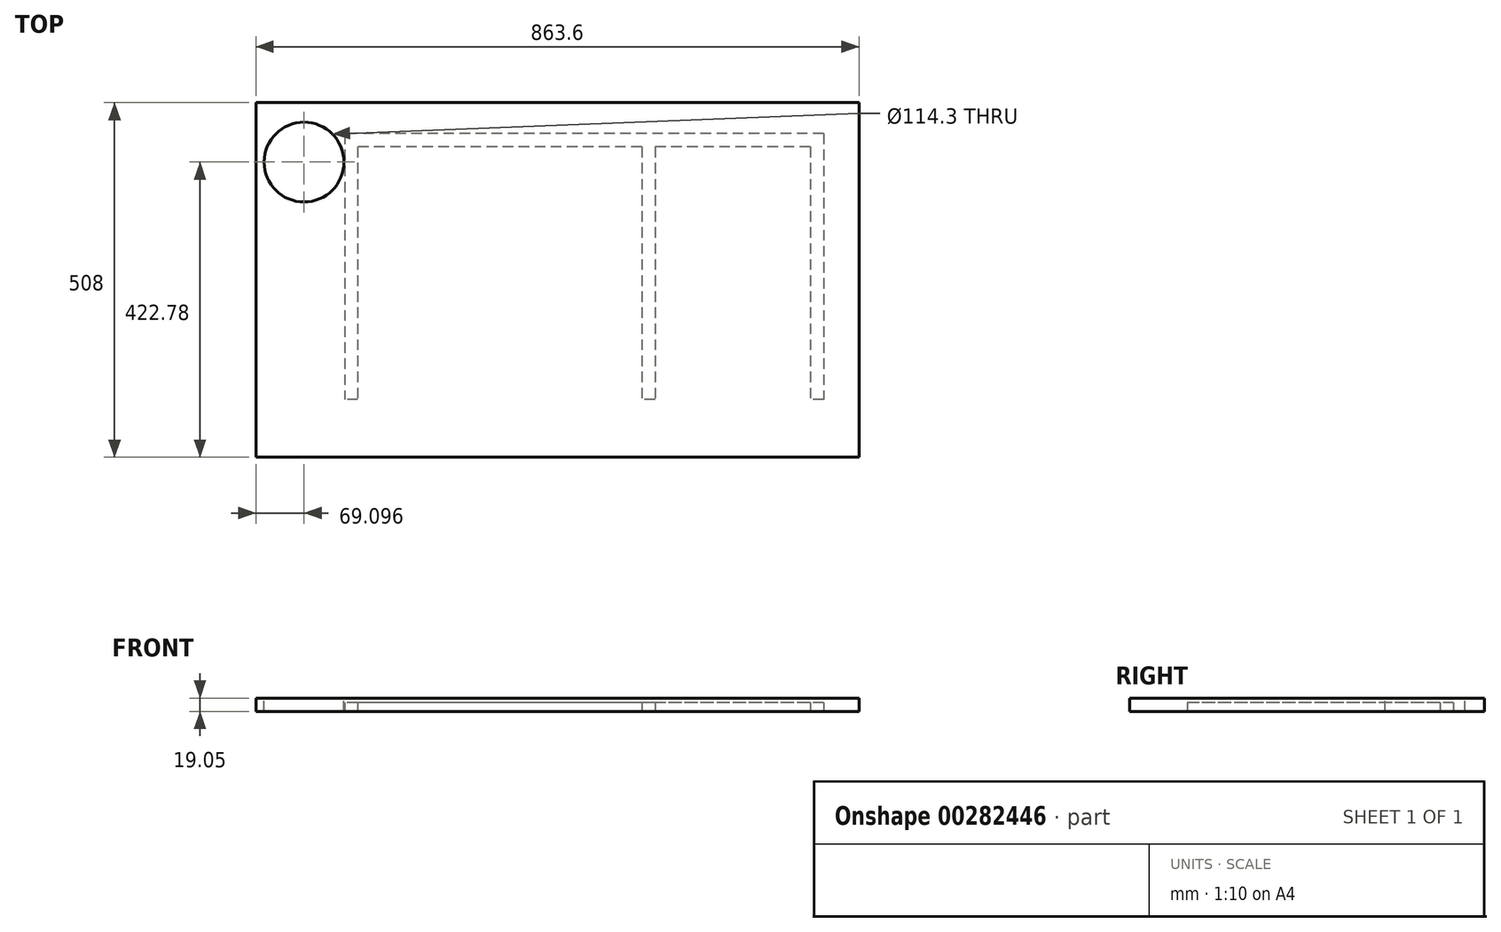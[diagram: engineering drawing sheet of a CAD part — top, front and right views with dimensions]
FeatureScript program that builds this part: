
annotation { "Feature Type Name" : "Feature", "Feature Type Description" : "" }
export const myFeature = defineFeature(function(context is Context, id is Id, definition is map)
    precondition{}
    {
        {
            var Q0;
            Q0=qCreatedBy(makeId("Top.planeOp"),FACE);
            var sketch = newSketch(context, id + "F0", { "sketchPlane" : qUnion([Q0])});
            skPoint(sketch, "E0.middle", {"position": v(0, 0) * mm});
            skLineSegment(sketch, "E1.bottom", {"start": v(-431.8, -254) * mm, "end": v(431.8, -254) * mm});
            skLineSegment(sketch, "E1.top", {"start": v(-431.8, 254) * mm, "end": v(431.8, 254) * mm});
            skLineSegment(sketch, "E1.left", {"start": v(-431.8, -254) * mm, "end": v(-431.8, 254) * mm});
            skLineSegment(sketch, "E1.right", {"start": v(431.8, -254) * mm, "end": v(431.8, 254) * mm});
            skSolve(sketch);
        }
        {
            var Q0;
            Q0 = qSketchRegion(id + "F0", true);
            extrude(context, id + "F1", {"entities" : qUnion([Q0]), "depth" : 19.05 * mm});
        }
        {
            var Q0;
            Q0=makeQuery(id+"F1.opExtrude","CAP_FACE",FACE,{"disambiguationData":[OSD([sQuery(id+"F0.wireOp",EDGE,"E1.bottom"),sQuery(id+"F0.wireOp",EDGE,"E1.top"),sQuery(id+"F0.wireOp",EDGE,"E1.left"),sQuery(id+"F0.wireOp",EDGE,"E1.right")])],"isStart":true});
            var sketch = newSketch(context, id + "F2", { "sketchPlane" : qUnion([Q0])});
            skLineSegment(sketch, "E2", {"start": v(0, -254) * mm, "end": v(0, 254) * mm, "construction": true});
            skLineSegment(sketch, "E3", {"start": v(431.8, 0) * mm, "end": v(-431.8, 0) * mm, "construction": true});
            skLineSegment(sketch, "E4", {"start": v(431.8, -254) * mm, "end": v(431.8, -209.55) * mm, "construction": true});
            skLineSegment(sketch, "E5", {"start": v(431.8, -209.55) * mm, "end": v(-431.8, -209.55) * mm, "construction": true});
            skLineSegment(sketch, "E6", {"start": v(431.8, -171.75) * mm, "end": v(381, -171.75) * mm, "construction": true});
            skLineSegment(sketch, "E7", {"start": v(381, -254) * mm, "end": v(381, 254) * mm, "construction": true});
            skLineSegment(sketch, "E8", {"start": v(-431.8, -119.08) * mm, "end": v(-304.8, -119.08) * mm, "construction": true});
            skLineSegment(sketch, "E9", {"start": v(-304.8, -254) * mm, "end": v(-304.8, 254) * mm, "construction": true});
            skLineSegment(sketch, "E10.bottom", {"start": v(381, -209.55) * mm, "end": v(-304.8, -209.55) * mm});
            skLineSegment(sketch, "E10.top", {"start": v(381, -190.5) * mm, "end": v(-304.8, -190.5) * mm});
            skLineSegment(sketch, "E10.left", {"start": v(381, -209.55) * mm, "end": v(381, -190.5) * mm});
            skLineSegment(sketch, "E10.right", {"start": v(-304.8, -209.55) * mm, "end": v(-304.8, -190.5) * mm});
            skLineSegment(sketch, "E11", {"start": v(38.1, -209.55) * mm, "end": v(38.1, -190.5) * mm, "construction": true});
            skLineSegment(sketch, "E12.bottom", {"start": v(-285.75, -190.5) * mm, "end": v(-304.8, -190.5) * mm});
            skLineSegment(sketch, "E12.top", {"start": v(-285.75, 171.45) * mm, "end": v(-304.8, 171.45) * mm});
            skLineSegment(sketch, "E12.left", {"start": v(-285.75, -190.5) * mm, "end": v(-285.75, 171.45) * mm});
            skLineSegment(sketch, "E12.right", {"start": v(-304.8, -190.5) * mm, "end": v(-304.8, 171.45) * mm});
            skLineSegment(sketch, "E13", {"start": v(-285.75, -74.88) * mm, "end": v(120.65, -74.88) * mm, "construction": true});
            skLineSegment(sketch, "E14", {"start": v(120.65, -190.5) * mm, "end": v(120.65, 254) * mm, "construction": true});
            skLineSegment(sketch, "E15.bottom", {"start": v(139.7, -190.5) * mm, "end": v(120.65, -190.5) * mm});
            skLineSegment(sketch, "E15.top", {"start": v(139.7, 171.45) * mm, "end": v(120.65, 171.45) * mm});
            skLineSegment(sketch, "E15.left", {"start": v(139.7, -190.5) * mm, "end": v(139.7, 171.45) * mm});
            skLineSegment(sketch, "E15.right", {"start": v(120.65, -190.5) * mm, "end": v(120.65, 171.45) * mm});
            skLineSegment(sketch, "E16.bottom", {"start": v(381, -190.5) * mm, "end": v(361.95, -190.5) * mm});
            skLineSegment(sketch, "E16.top", {"start": v(381, 171.45) * mm, "end": v(361.95, 171.45) * mm});
            skLineSegment(sketch, "E16.left", {"start": v(381, -190.5) * mm, "end": v(381, 171.45) * mm});
            skLineSegment(sketch, "E16.right", {"start": v(361.95, -190.5) * mm, "end": v(361.95, 171.45) * mm});
            skLineSegment(sketch, "E17", {"start": v(361.95, -85.73) * mm, "end": v(139.7, -85.73) * mm, "construction": true});
            skSolve(sketch);
        }
        {
            var Q0;
            Q0 = qSketchRegion(id + "F2", true);
            extrude(context, id + "F3", {"entities" : qUnion([Q0]), "operationType" : NewBodyOperationType.REMOVE, "oppositeDirection" : true, "depth" : 12.7 * mm});
        }
        {
            var Q0;
            Q0=makeQuery(id+"F1.opExtrude","CAP_FACE",FACE,{"disambiguationData":[OSD([sQuery(id+"F0.wireOp",EDGE,"E1.bottom"),sQuery(id+"F0.wireOp",EDGE,"E1.top"),sQuery(id+"F0.wireOp",EDGE,"E1.left"),sQuery(id+"F0.wireOp",EDGE,"E1.right")])],"isStart":false});
            var sketch = newSketch(context, id + "F4", { "sketchPlane" : qUnion([Q0])});
            skCircle(sketch, "E18", {"center": v(-362.7, 168.78) * mm, "radius": 57.15 * mm});
            skSolve(sketch);
        }
        {
            var Q0;
            Q0=makeQuery(id+"F4.imprint","IMPRINT",FACE,{"disambiguationData":[TD([[makeQuery(id+"F4.imprint","IMPRINT",EDGE,{"derivedFrom":sQuery(id+"F4.wireOp",EDGE,"E18")}),1.0]])]});
            extrude(context, id + "F5", {"entities" : qUnion([Q0]), "operationType" : NewBodyOperationType.REMOVE, "oppositeDirection" : true, "depth" : 25.4 * mm});
        }
    });
